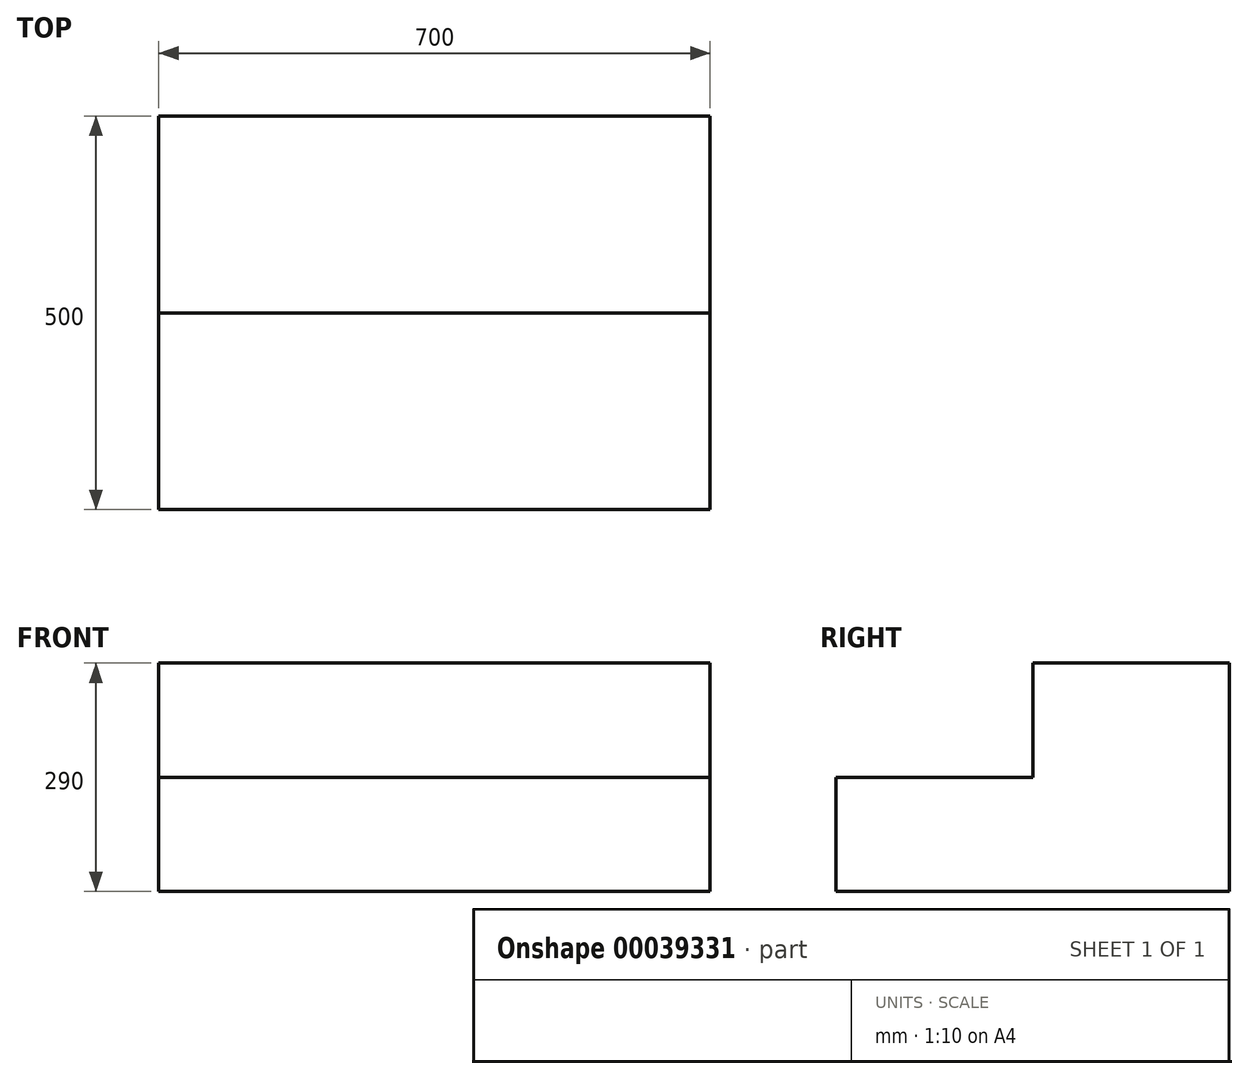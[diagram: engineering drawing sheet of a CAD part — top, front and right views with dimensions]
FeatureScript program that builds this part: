
annotation { "Feature Type Name" : "Feature", "Feature Type Description" : "" }
export const myFeature = defineFeature(function(context is Context, id is Id, definition is map)
    precondition{}
    {
        {
            var Q0;
            Q0=qCreatedBy(makeId("Right.planeOp"),FACE);
            var sketch = newSketch(context, id + "F0", { "sketchPlane" : qUnion([Q0])});
            skLineSegment(sketch, "E0", {"start": v(0, 0) * mm, "end": v(0, 290) * mm});
            skLineSegment(sketch, "E1", {"start": v(0, 290) * mm, "end": v(-250, 290) * mm});
            skLineSegment(sketch, "E2", {"start": v(-250, 290) * mm, "end": v(-250, 145) * mm});
            skLineSegment(sketch, "E3", {"start": v(-250, 145) * mm, "end": v(-500, 145) * mm});
            skLineSegment(sketch, "E4", {"start": v(-500, 145) * mm, "end": v(-500, 0) * mm});
            skLineSegment(sketch, "E5", {"start": v(-500, 0) * mm, "end": v(0, 0) * mm});
            skSolve(sketch);
        }
        {
            var Q0;
            Q0=makeQuery(id+"F0.imprint","IMPRINT",FACE,{"disambiguationData":[TD([[makeQuery(id+"F0.imprint","IMPRINT",EDGE,{"derivedFrom":sQuery(id+"F0.wireOp",EDGE,"E0")}),1.0]])]});
            extrude(context, id + "F1", {"entities" : qUnion([Q0]), "depth" : 700 * mm});
        }
    });
